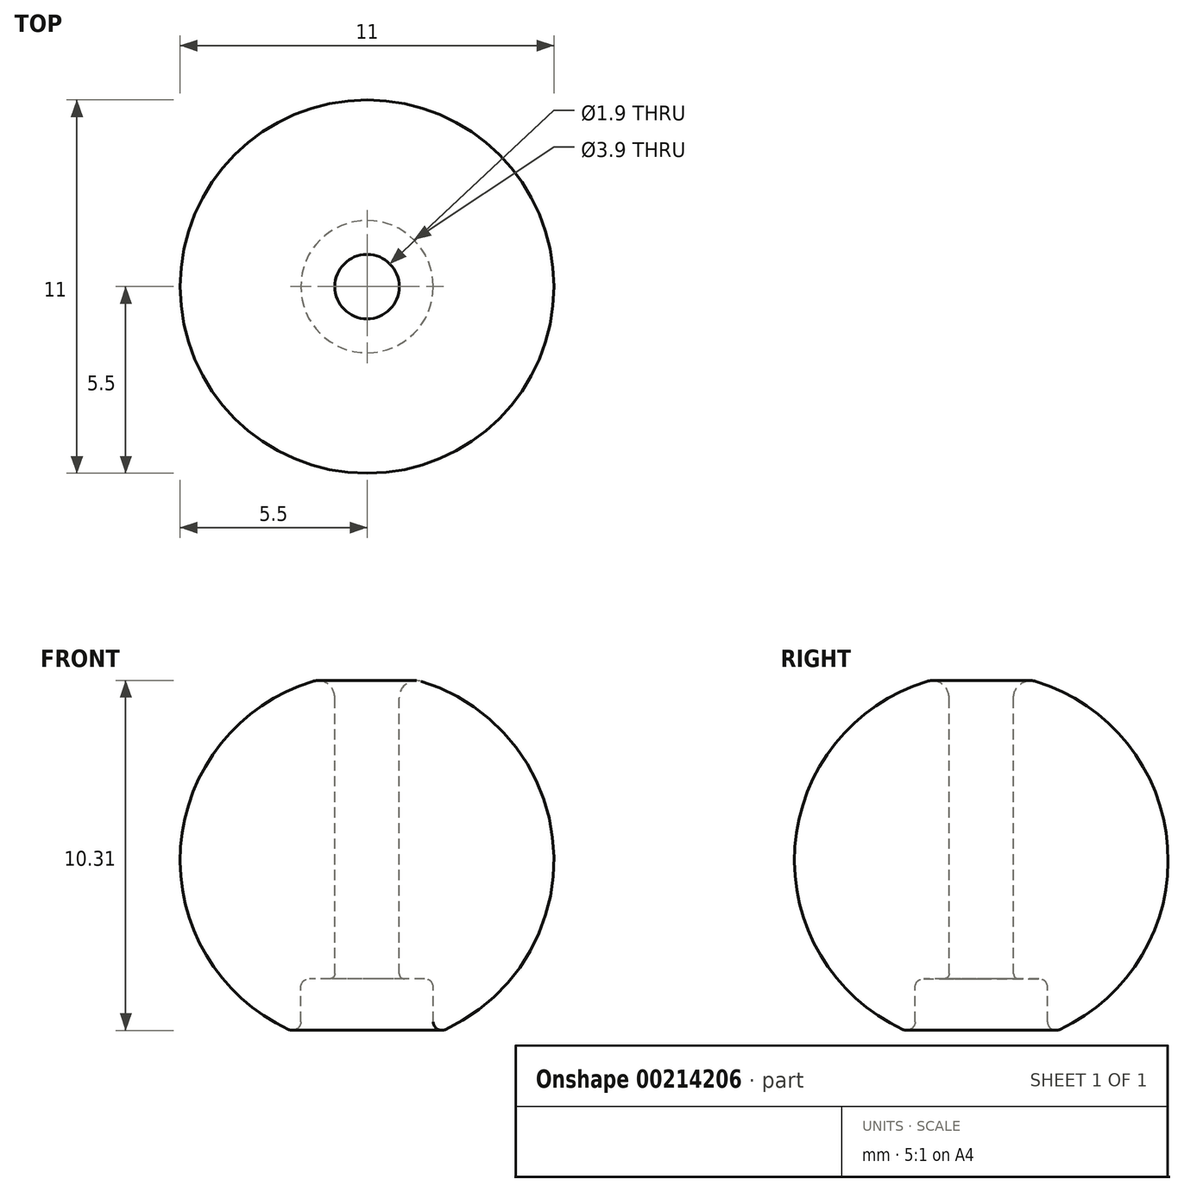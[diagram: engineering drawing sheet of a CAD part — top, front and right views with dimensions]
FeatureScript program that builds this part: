
annotation { "Feature Type Name" : "Feature", "Feature Type Description" : "" }
export const myFeature = defineFeature(function(context is Context, id is Id, definition is map)
    precondition{}
    {
        {
            var Q0;
            Q0=qCreatedBy(makeId("Front.planeOp"),FACE);
            var sketch = newSketch(context, id + "F0", { "sketchPlane" : qUnion([Q0])});
            skLineSegment(sketch, "E0", {"start": v(0, 12.7) * mm, "end": v(0, -11.2) * mm, "construction": true});
            skArc(sketch, "E1", {"start": v(-1.6, 5.26) * mm, "mid": v(-5.49, 0.38) * mm, "end": v(-2.3, -5) * mm});
            skLineSegment(sketch, "E2", {"start": v(-0.95, 4.79) * mm, "end": v(-0.95, -3.35) * mm});
            skLineSegment(sketch, "E3", {"start": v(-1.1, -3.5) * mm, "end": v(-1.7, -3.5) * mm});
            skLineSegment(sketch, "E4", {"start": v(-1.95, -3.75) * mm, "end": v(-1.95, -4.77) * mm});
            skArc(sketch, "E5.filletArc", {"start": v(-0.95, 4.79) * mm, "mid": v(-1.15, 5.19) * mm, "end": v(-1.6, 5.26) * mm});
            skPoint(sketch, "E6.orphan", {"position": v(0, -5.5) * mm});
            skPoint(sketch, "E7.visualSharp", {"position": v(-1.95, -5.14) * mm});
            skArc(sketch, "E7.filletArc", {"start": v(-2.3, -5) * mm, "mid": v(-2.07, -4.98) * mm, "end": v(-1.95, -4.77) * mm});
            skPoint(sketch, "E8.visualSharp", {"position": v(-0.95, -3.5) * mm});
            skArc(sketch, "E8.filletArc", {"start": v(-1.1, -3.5) * mm, "mid": v(-1, -3.46) * mm, "end": v(-0.95, -3.35) * mm});
            skPoint(sketch, "E9.visualSharp", {"position": v(-1.95, -3.5) * mm});
            skArc(sketch, "E9.filletArc", {"start": v(-1.7, -3.5) * mm, "mid": v(-1.88, -3.57) * mm, "end": v(-1.95, -3.75) * mm});
            skSolve(sketch);
        }
        {
            var Q0;
            Q0=makeQuery(id+"F0.imprint","IMPRINT",FACE,{"disambiguationData":[TD([[makeQuery(id+"F0.imprint","IMPRINT",EDGE,{"derivedFrom":sQuery(id+"F0.wireOp",EDGE,"E1")}),1.0]])]});
            var Q1;
            Q1=sQuery(id+"F0.wireOp",EDGE,"E0");
            revolve(context, id + "F1", {"entities" : qUnion([Q0]), "axis" : qUnion([Q1]), "revolveType" : RevolveType.FULL});
        }
    });
